# Revit family: Zumtobel SLOTLIGHT INF slim CL
name_source: partatom
category: Lighting Fixtures
revit_build: Autodesk Revit 2016 (Build: 20150220_1215(x64)
units: mm (PartAtom-declared; Revit-internal decimal feet)

## family parameters
Cut with Voids When Loaded = No
Host = Face
Light Source = Yes
OmniClass Number = 23.80.70.11
OmniClass Title = Luminaries for Internal Lighting
Part Type = Normal
Room Calculation Point = No
Round Connector Dimension = Use Diameter
Shared = No

## types (1)
- SLOIN slim CL LED2400 L775
    Apparent Load = 91 VA
    Assembly Code = D5020200
    Body = Zumtobel_Metal_White
    Color Filter = 16777215
    Color Light Emitting Surface = Zumtobel_PMMA_White
    Default Elevation = 0 mm  [stored 0 ft]
    Description = SLOTLIGHT infinity slim corner luminaire
    Dimming Lamp Color Temperature Shift = <None>
    Emit Shape Visible in Rendering = No
    Emit from Rectangle Length = 45 mm  [stored 0.147638 ft]
    Emit from Rectangle Width = 775 mm  [stored 2.54265 ft]
    Height = 64 mm  [stored 0.209974 ft]
    Lamp = LED
    Length = 775 mm  [stored 2.54265 ft]
    Manufacturer = Zumtobel Lighting
    Model = 42183998
    Photometric Web File = 42183998.IES
    Tilt Angle = -90.00°
    URL = http://www.zumtobel.com
    Width = 45 mm  [stored 0.147638 ft]

note: [stored X ft] marks values corroborated as IEEE doubles in the binary element streams (Revit-internal decimal feet)

## geometry (parser evidence)
native form markers: Blend x28, Sweep x7
no freeform markers — native parametric forms only
